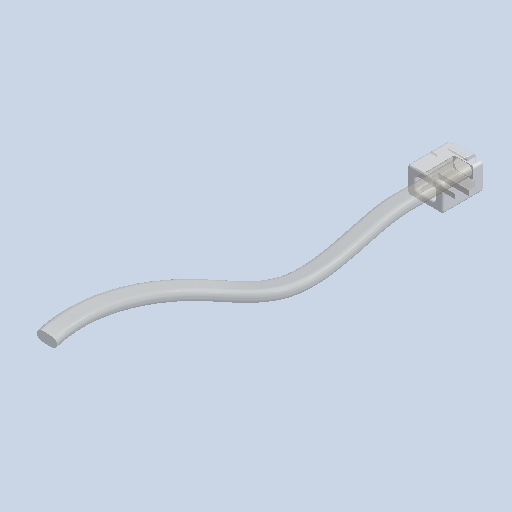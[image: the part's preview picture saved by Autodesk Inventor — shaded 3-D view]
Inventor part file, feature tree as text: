
AUTODESK INVENTOR PART (.ipt)
format: ipt  version: 2022.1 (Build 261234000, 234)  size: 337,920 bytes
history: mixed  units: mm (DEFAULTED — no unit token found)
features: other x8, sweep x1, imported_body x1
bodies: Body1 (imported_parasolid)
feature tree (10):
  other  "Sólido1"
  other  "Origen"
  other  "Plano YZ"
  other  "Plano XZ"
  other  "Plano XY"
  other  "Eje X"
  other  "Eje Y"
  other  "Eje Z"
  sweep  "Sweep1"
  imported_body  NMx_Import_Brep_tag  [imported B-rep: ~10 faces, bbox_mm=[3.39847, 0.369177, 6.299097]]
